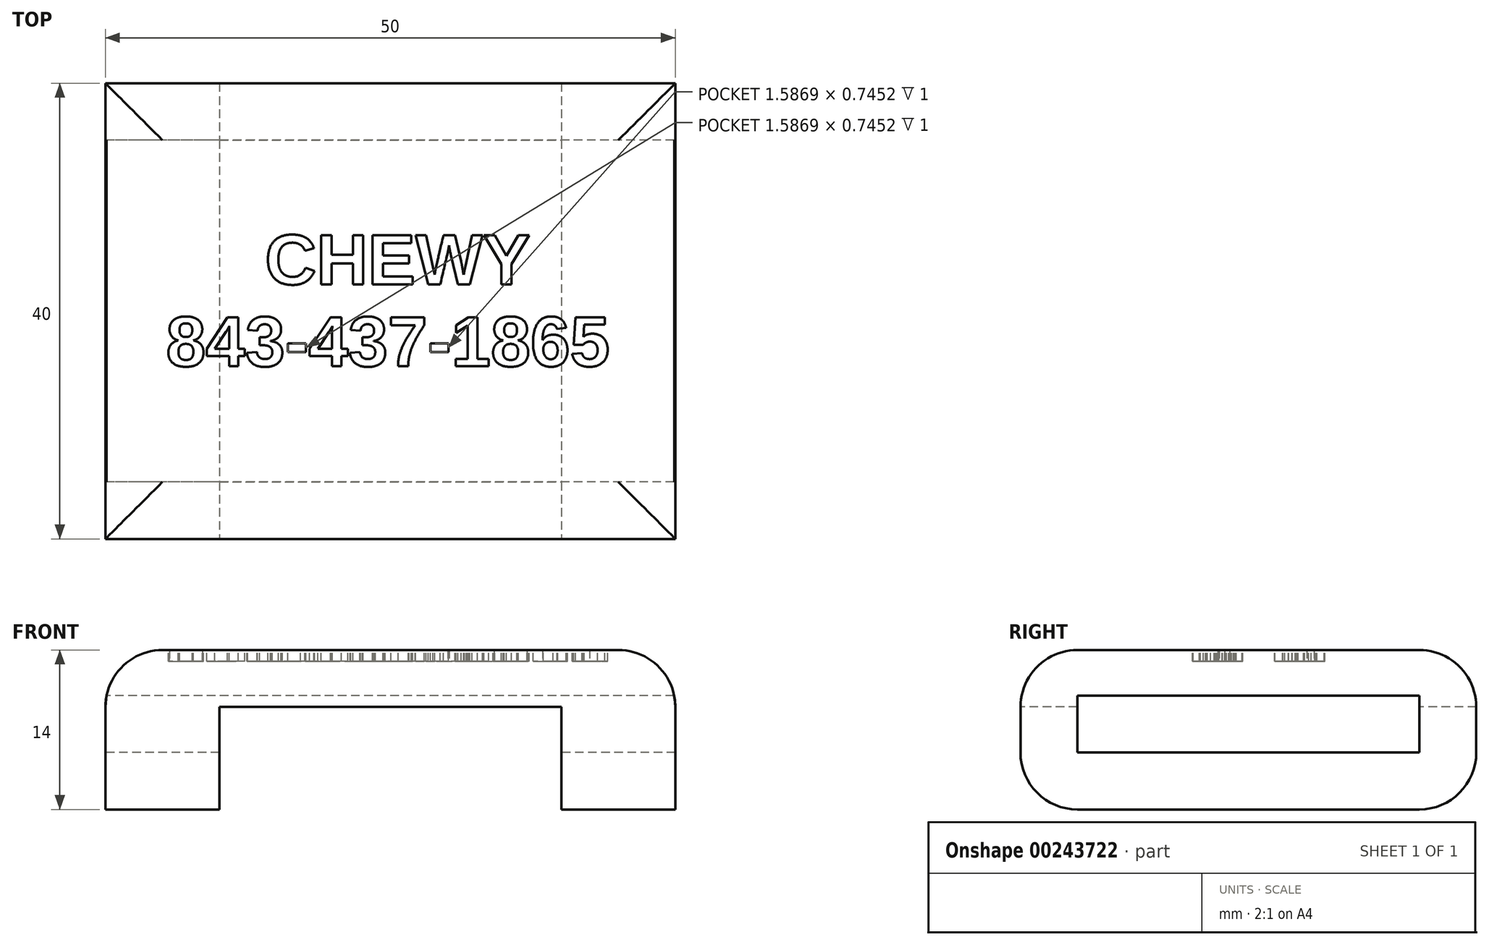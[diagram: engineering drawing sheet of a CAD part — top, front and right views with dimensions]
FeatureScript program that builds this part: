
annotation { "Feature Type Name" : "Feature", "Feature Type Description" : "" }
export const myFeature = defineFeature(function(context is Context, id is Id, definition is map)
    precondition{}
    {
        {
            var Q0;
            Q0=qCreatedBy(makeId("Top.planeOp"),FACE);
            var sketch = newSketch(context, id + "F0", { "sketchPlane" : qUnion([Q0])});
            skLineSegment(sketch, "E0.bottom", {"start": v(-25, 20) * mm, "end": v(25, 20) * mm});
            skLineSegment(sketch, "E0.top", {"start": v(-25, -20) * mm, "end": v(25, -20) * mm});
            skLineSegment(sketch, "E0.left", {"start": v(-25, 20) * mm, "end": v(-25, -20) * mm});
            skLineSegment(sketch, "E0.right", {"start": v(25, 20) * mm, "end": v(25, -20) * mm});
            skPoint(sketch, "E0.middle", {"position": v(0, 0) * mm});
            skSolve(sketch);
        }
        {
            var Q0;
            Q0 = qSketchRegion(id + "F0", true);
            extrude(context, id + "F1", {"entities" : qUnion([Q0]), "depth" : 14 * mm});
        }
        {
            var Q0;
            Q0=makeQuery(id+"F1.opExtrude","SWEPT_FACE",FACE,{"disambiguationData":[OSD([sQuery(id+"F0.wireOp",EDGE,"E0.left")])]});
            var sketch = newSketch(context, id + "F2", { "sketchPlane" : qUnion([Q0])});
            skLineSegment(sketch, "E1.bottom", {"start": v(-15, 5) * mm, "end": v(15, 5) * mm});
            skLineSegment(sketch, "E1.top", {"start": v(-15, 10) * mm, "end": v(15, 10) * mm});
            skLineSegment(sketch, "E1.left", {"start": v(-15, 5) * mm, "end": v(-15, 10) * mm});
            skLineSegment(sketch, "E1.right", {"start": v(15, 5) * mm, "end": v(15, 10) * mm});
            skPoint(sketch, "E1.middle", {"position": v(0, 7.5) * mm});
            skSolve(sketch);
        }
        {
            var Q0;
            Q0=makeQuery(id+"F2.imprint","IMPRINT",FACE,{"disambiguationData":[TD([[makeQuery(id+"F2.imprint","IMPRINT",EDGE,{"derivedFrom":sQuery(id+"F2.wireOp",EDGE,"E1.bottom")}),1.0]])]});
            extrude(context, id + "F3", {"entities" : qUnion([Q0]), "operationType" : NewBodyOperationType.REMOVE, "oppositeDirection" : true, "depth" : 50 * mm});
        }
        {
            var Q0;
            Q0=makeQuery(id+"F1.opExtrude","SWEPT_FACE",FACE,{"disambiguationData":[OSD([sQuery(id+"F0.wireOp",EDGE,"E0.top")])]});
            var sketch = newSketch(context, id + "F4", { "sketchPlane" : qUnion([Q0])});
            skLineSegment(sketch, "E2.bottom", {"start": v(-15, 9) * mm, "end": v(15, 9) * mm});
            skLineSegment(sketch, "E2.top", {"start": v(-15, -9) * mm, "end": v(15, -9) * mm});
            skLineSegment(sketch, "E2.left", {"start": v(-15, 9) * mm, "end": v(-15, -9) * mm});
            skLineSegment(sketch, "E2.right", {"start": v(15, 9) * mm, "end": v(15, -9) * mm});
            skPoint(sketch, "E2.middle", {"position": v(0, 0) * mm});
            skSolve(sketch);
        }
        {
            var Q0;
            Q0 = qSketchRegion(id + "F4", true);
            var Q1;
            Q1=makeQuery(id+"F1.opExtrude","SWEPT_FACE",FACE,{"disambiguationData":[OSD([sQuery(id+"F0.wireOp",EDGE,"E0.bottom")])]});
            extrude(context, id + "F5", {"entities" : qUnion([Q0]), "operationType" : NewBodyOperationType.REMOVE, "endBound" : BoundingType.UP_TO_SURFACE, "oppositeDirection" : true, "endBoundEntityFace" : qUnion([Q1]), "depth" : 30 * mm});
        }
        {
            var Q0;
            Q0=makeQuery(id+"F1.opExtrude","CAP_FACE",FACE,{"disambiguationData":[OSD([sQuery(id+"F0.wireOp",EDGE,"E0.bottom"),sQuery(id+"F0.wireOp",EDGE,"E0.top"),sQuery(id+"F0.wireOp",EDGE,"E0.left"),sQuery(id+"F0.wireOp",EDGE,"E0.right")])],"isStart":false});
            var Q1;
            {var subQ0=sQuery(id+"F0.wireOp",EDGE,"E0.bottom");var subQ1=sQuery(id+"F0.wireOp",EDGE,"E0.left");Q1=makeQuery(id+"F5.boolean.opBoolean","SPLIT",EDGE,{"disambiguationData":[TD([makeQuery(id+"F1.opExtrude","SWEPT_FACE",FACE,{"disambiguationData":[OSD([subQ1])]})])],"derivedFrom":makeQuery(id+"F1.opExtrude","CAP_EDGE",EDGE,{"disambiguationData":[OSD([subQ0])],"isStart":true})});}
            var Q2;
            {var subQ0=sQuery(id+"F0.wireOp",EDGE,"E0.bottom");var subQ1=sQuery(id+"F0.wireOp",EDGE,"E0.right");Q2=makeQuery(id+"F5.boolean.opBoolean","SPLIT",EDGE,{"disambiguationData":[TD([makeQuery(id+"F1.opExtrude","SWEPT_FACE",FACE,{"disambiguationData":[OSD([subQ1])]})])],"derivedFrom":makeQuery(id+"F1.opExtrude","CAP_EDGE",EDGE,{"disambiguationData":[OSD([subQ0])],"isStart":true})});}
            var Q3;
            {var subQ0=sQuery(id+"F0.wireOp",EDGE,"E0.left");var subQ1=sQuery(id+"F0.wireOp",EDGE,"E0.top");Q3=makeQuery(id+"F5.boolean.opBoolean","SPLIT",EDGE,{"disambiguationData":[TD([makeQuery(id+"F1.opExtrude","SWEPT_FACE",FACE,{"disambiguationData":[OSD([subQ0])]})])],"derivedFrom":makeQuery(id+"F1.opExtrude","CAP_EDGE",EDGE,{"disambiguationData":[OSD([subQ1])],"isStart":true})});}
            var Q4;
            {var subQ0=sQuery(id+"F0.wireOp",EDGE,"E0.right");var subQ1=sQuery(id+"F0.wireOp",EDGE,"E0.top");Q4=makeQuery(id+"F5.boolean.opBoolean","SPLIT",EDGE,{"disambiguationData":[TD([makeQuery(id+"F1.opExtrude","SWEPT_FACE",FACE,{"disambiguationData":[OSD([subQ0])]})])],"derivedFrom":makeQuery(id+"F1.opExtrude","CAP_EDGE",EDGE,{"disambiguationData":[OSD([subQ1])],"isStart":true})});}
            fillet(context, id + "F6", {"entities" : qUnion([Q0, Q1, Q2, Q3, Q4]), "radius" : 5 * mm, "tangentPropagation" : true, "allowEdgeOverflow" : false});
        }
        {
            var Q0;
            Q0=qCreatedBy(makeId("Top.planeOp"),FACE);
            cPlane(context, id + "F7", {"entities" : qUnion([Q0]), "cplaneType" : CPlaneType.OFFSET, "offset" : 14 * mm, "width" : 150 * mm, "height" : 150 * mm});
        }
        {
            var Q0;
            Q0=qCreatedBy(id+"F7.planeOp",FACE);
            var sketch = newSketch(context, id + "F8", { "sketchPlane" : qUnion([Q0])});
            skText(sketch, "E3", { "text": "     CHEWY\n843-437-1865", "fontName": "Arimo-Bold.ttf"});
            const initialGuessF8  = {"E3": [-0.01968, 0.00235, 1, 0, 0.0045]};
            skSetInitialGuess(sketch, initialGuessF8);
            skSolve(sketch);
        }
        {
            var Q0;
            Q0 = qSketchRegion(id + "F8", true);
            extrude(context, id + "F9", {"entities" : qUnion([Q0]), "operationType" : NewBodyOperationType.REMOVE, "oppositeDirection" : true, "depth" : 1 * mm});
        }
    });
